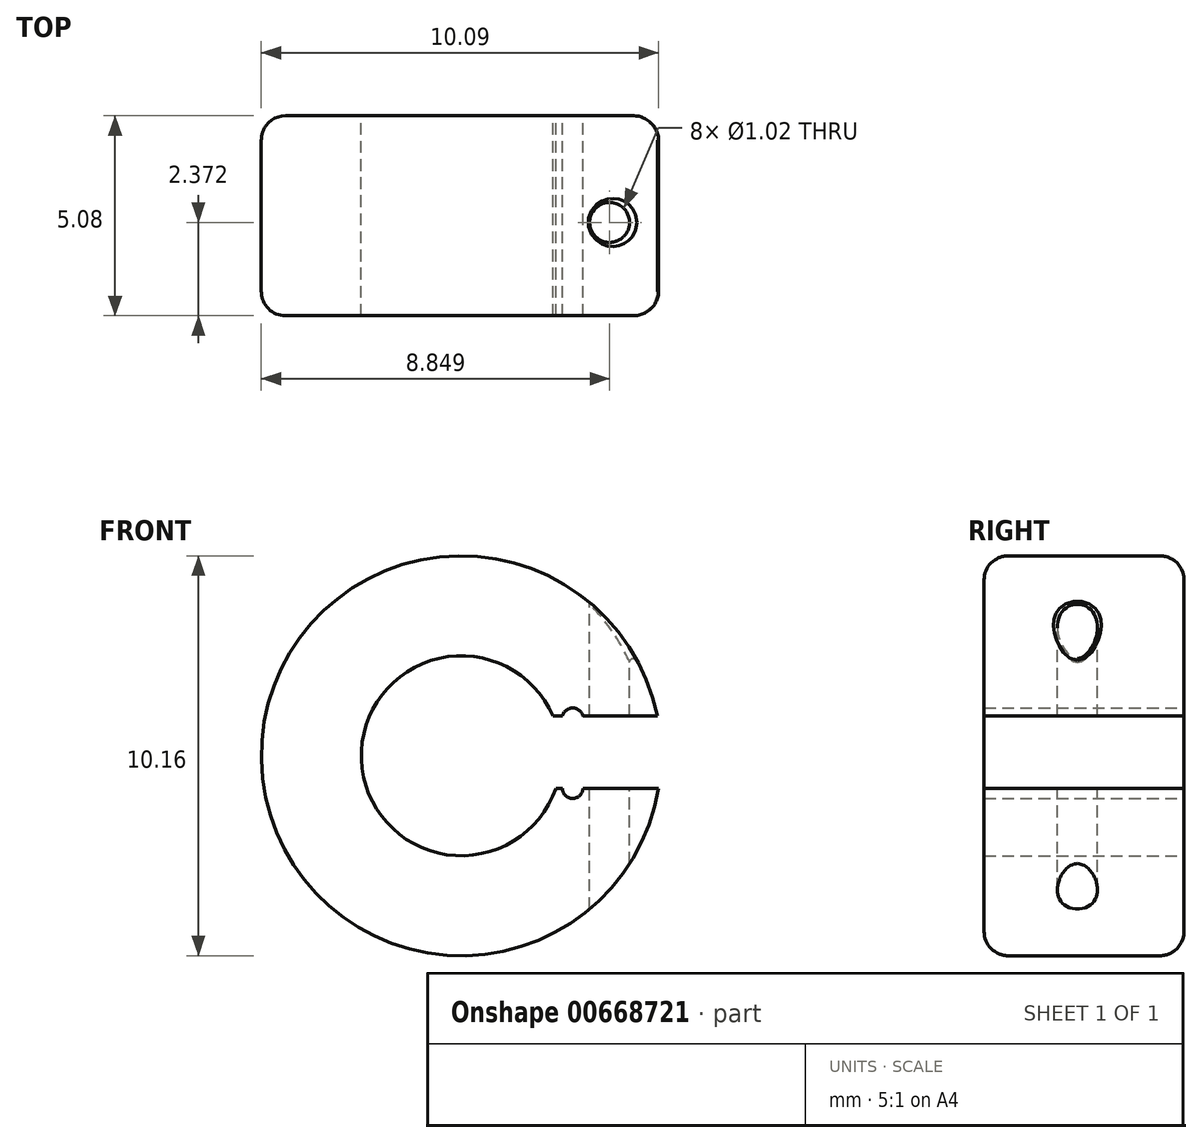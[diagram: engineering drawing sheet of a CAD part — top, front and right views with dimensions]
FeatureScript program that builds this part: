
annotation { "Feature Type Name" : "Feature", "Feature Type Description" : "" }
export const myFeature = defineFeature(function(context is Context, id is Id, definition is map)
    precondition{}
    {
        {
            var Q0;
            Q0=qCreatedBy(makeId("Front.planeOp"),FACE);
            var sketch = newSketch(context, id + "F0", { "sketchPlane" : qUnion([Q0])});
            skArc(sketch, "E0", {"start": v(2.33, 1) * mm, "mid": v(-2.54, -0.1) * mm, "end": v(2.4, -0.82) * mm});
            skArc(sketch, "E1", {"start": v(4.98, 1) * mm, "mid": v(-5.08, -0.1) * mm, "end": v(5.01, -0.82) * mm});
            skLineSegment(sketch, "E2", {"start": v(2.33, 1) * mm, "end": v(2.57, 1) * mm});
            skLineSegment(sketch, "E3", {"start": v(2.4, -0.82) * mm, "end": v(2.57, -0.82) * mm});
            skArc(sketch, "E4", {"start": v(3.1, 1) * mm, "mid": v(2.83, 1.21) * mm, "end": v(2.57, 1) * mm});
            skArc(sketch, "E5", {"start": v(2.57, -0.82) * mm, "mid": v(2.83, -1.09) * mm, "end": v(3.1, -0.82) * mm});
            skLineSegment(sketch, "E6.trimOffspring", {"start": v(3.1, 1) * mm, "end": v(4.98, 1) * mm});
            skLineSegment(sketch, "E7.trimOffspring", {"start": v(3.1, -0.82) * mm, "end": v(5.01, -0.82) * mm});
            skSolve(sketch);
        }
        {
            var Q0;
            Q0=makeQuery(id+"F0.imprint","IMPRINT",FACE,{"disambiguationData":[TD([[makeQuery(id+"F0.imprint","IMPRINT",EDGE,{"derivedFrom":sQuery(id+"F0.wireOp",EDGE,"E0")}),-1.0]])]});
            extrude(context, id + "F1", {"entities" : qUnion([Q0]), "depth" : 5.08 * mm, "offsetDistance" : 25.4 * mm});
        }
        {
            var Q0;
            Q0=qCreatedBy(makeId("Top.planeOp"),FACE);
            var sketch = newSketch(context, id + "F2", { "sketchPlane" : qUnion([Q0])});
            skCircle(sketch, "E8", {"center": v(3.77, -2.7) * mm, "radius": 0.5 * mm});
            skSolve(sketch);
        }
        {
            var Q0;
            Q0=makeQuery(id+"F2.imprint","IMPRINT",FACE,{"disambiguationData":[TD([[makeQuery(id+"F2.imprint","IMPRINT",EDGE,{"derivedFrom":sQuery(id+"F2.wireOp",EDGE,"E8")}),1.0]])]});
            extrude(context, id + "F3", {"entities" : qUnion([Q0]), "operationType" : NewBodyOperationType.REMOVE, "endBound" : BoundingType.SYMMETRIC, "oppositeDirection" : true, "depth" : 25.4 * mm, "offsetDistance" : 25.4 * mm});
        }
        {
            var Q0;
            Q0=makeQuery(id+"F3.boolean.opBoolean","INTERSECT",EDGE,{"disambiguationData":[OD(0.0)],"derivedFrom":[makeQuery(id+"F1.opExtrude","SWEPT_FACE",FACE,{"disambiguationData":[OSD([sQuery(id+"F0.wireOp",EDGE,"E1")])]}),makeQuery(id+"F3.opExtrude","SWEPT_FACE",FACE,{"disambiguationData":[OSD([sQuery(id+"F2.wireOp",EDGE,"E8")])]})]});
            fillet(context, id + "F4", {"entities" : qUnion([Q0]), "radius" : 0.1 * mm, "tangentPropagation" : true, "allowEdgeOverflow" : false});
        }
        {
            var Q0;
            Q0=makeQuery(id+"F1.opExtrude","CAP_EDGE",EDGE,{"disambiguationData":[OSD([sQuery(id+"F0.wireOp",EDGE,"E1")])],"isStart":false});
            var Q1;
            Q1=makeQuery(id+"F1.opExtrude","CAP_EDGE",EDGE,{"disambiguationData":[OSD([sQuery(id+"F0.wireOp",EDGE,"E1")])],"isStart":true});
            fillet(context, id + "F5", {"entities" : qUnion([Q0, Q1]), "radius" : 0.61 * mm, "tangentPropagation" : true, "allowEdgeOverflow" : false});
        }
    });
